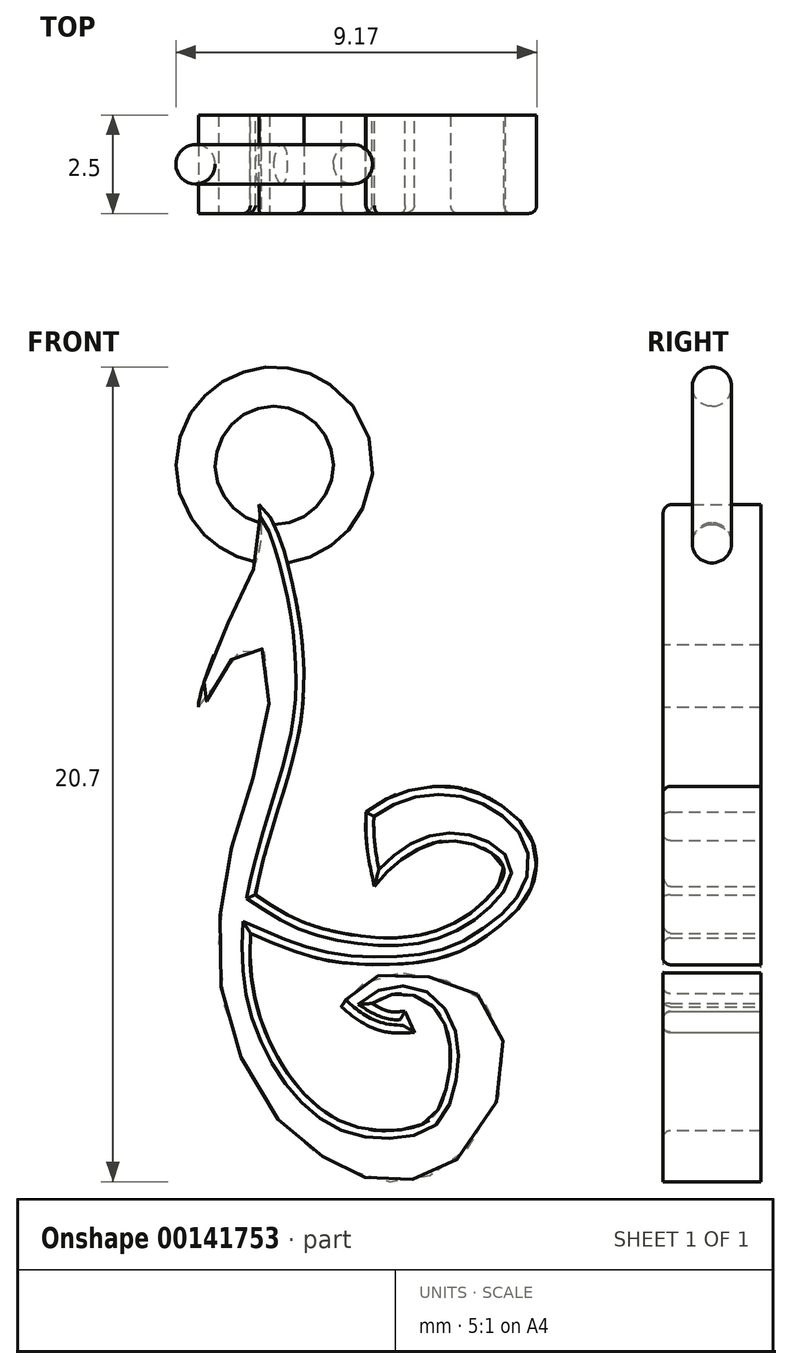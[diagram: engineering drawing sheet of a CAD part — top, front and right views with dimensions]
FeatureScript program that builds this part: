
annotation { "Feature Type Name" : "Feature", "Feature Type Description" : "" }
export const myFeature = defineFeature(function(context is Context, id is Id, definition is map)
    precondition{}
    {
        {
            var Q0;
            Q0=qCreatedBy(makeId("Front.planeOp"),FACE);
            var sketch = newSketch(context, id + "F0", { "sketchPlane" : qUnion([Q0])});
            skLineSegment(sketch, "E0.bottom", {"start": v(-7.5, 0) * mm, "end": v(9.5, 0) * mm, "construction": true});
            skLineSegment(sketch, "E0.top", {"start": v(-7.5, 17) * mm, "end": v(9.5, 17) * mm, "construction": true});
            skLineSegment(sketch, "E0.left", {"start": v(-7.5, 0) * mm, "end": v(-7.5, 17) * mm, "construction": true});
            skLineSegment(sketch, "E0.right", {"start": v(9.5, 0) * mm, "end": v(9.5, 17) * mm, "construction": true});
            skLineSegment(sketch, "E1", {"start": v(0, 0) * mm, "end": v(0, 23.23) * mm, "construction": true});
            skFitSpline(sketch, "E2", {"points": [v(-1.83, 17) * mm, v(-1.82, 15.9) * mm, v(-2.39, 14.45) * mm, v(-3.04, 13.02) * mm, v(-3.35, 11.84) * mm, v(-3.09, 12.13) * mm, v(-2.54, 13.05) * mm, v(-1.94, 13.43) * mm, v(-1.68, 13.22) * mm, v(-1.63, 11.44) * mm, v(-2.32, 9.03) * mm, v(-2.77, 6.94) * mm, v(-2.78, 4.69) * mm, v(-2.04, 2.45) * mm, v(-0.78, 0.82) * mm, v(0.2, 0.23) * mm, v(1.09, -0.16) * mm, v(2.12, -0.14) * mm, v(3.04, 0.23) * mm, v(4.24, 1.9) * mm, v(4.33, 3.53) * mm, v(3.7, 4.58) * mm, v(2.6, 4.98) * mm, v(1.43, 5.09) * mm, v(0.65, 4.7) * mm, v(0.26, 4.24) * mm], "startDerivative": vector(3.52, -28.57) * mm, "endDerivative": vector(-9.9, -17.08) * mm});
            skFitSpline(sketch, "E3", {"points": [v(0.26, 4.24) * mm, v(1.24, 3.64) * mm, v(2.12, 3.6) * mm], "startDerivative": vector(1.82, -1.62) * mm, "endDerivative": vector(1.77, 0.22) * mm});
            skLineSegment(sketch, "E4", {"start": v(2.12, 3.6) * mm, "end": v(1.89, 4.13) * mm});
            skFitSpline(sketch, "E5", {"points": [v(1.89, 4.13) * mm, v(1.46, 4.13) * mm, v(1.05, 4.33) * mm], "startDerivative": vector(-0.86, -0.08) * mm, "endDerivative": vector(-0.67, 0.39) * mm});
            skFitSpline(sketch, "E6", {"points": [v(1.05, 4.33) * mm, v(1.43, 4.53) * mm, v(2.2, 4.5) * mm, v(2.83, 3.93) * mm, v(3.04, 2.91) * mm, v(2.87, 1.98) * mm, v(2.5, 1.36) * mm, v(1.43, 1.1) * mm, v(0.23, 1.34) * mm, v(-0.95, 2.35) * mm, v(-1.8, 3.96) * mm, v(-2.06, 5.52) * mm, v(-1.92, 7.09) * mm, v(-1.38, 9.13) * mm, v(-0.75, 11.63) * mm, v(-0.8, 14.08) * mm, v(-1.14, 15.64) * mm, v(-1.44, 16.5) * mm, v(-1.83, 17) * mm], "startDerivative": vector(9.88, 7.94) * mm, "endDerivative": vector(-11.95, 7.75) * mm});
            skFitSpline(sketch, "E7", {"points": [v(-1.92, 7.09) * mm, v(-0.7, 6.4) * mm, v(1.22, 6) * mm, v(2.76, 6.2) * mm, v(3.76, 6.8) * mm, v(4.4, 7.67) * mm, v(4.1, 8.14) * mm, v(3.43, 8.42) * mm, v(2.66, 8.42) * mm, v(1.7, 7.91) * mm, v(1.1, 7.3) * mm], "startDerivative": vector(12.7, -8.61) * mm, "endDerivative": vector(-6.05, -7.17) * mm});
            skFitSpline(sketch, "E8", {"points": [v(1.1, 7.3) * mm, v(0.9, 8.5) * mm, v(0.9, 9.19) * mm], "startDerivative": vector(-0.46, 2.24) * mm, "endDerivative": vector(0.08, 1.5) * mm});
            skFitSpline(sketch, "E9", {"points": [v(-2.05, 6.11) * mm, v(-0.62, 5.55) * mm, v(0.65, 5.33) * mm, v(2.15, 5.37) * mm, v(3.39, 5.7) * mm, v(4.57, 6.55) * mm, v(5.04, 7.15) * mm, v(5.22, 7.9) * mm, v(4.96, 8.76) * mm, v(3.99, 9.56) * mm, v(2.88, 9.84) * mm, v(1.66, 9.64) * mm, v(0.9, 9.19) * mm], "startDerivative": vector(15.2, -6.57) * mm, "endDerivative": vector(-9.55, -6.77) * mm});
            skSolve(sketch);
        }
        {
            var Q0;
            Q0=qSketchRegion(id+"F0",true);
            extrude(context, id + "F1", {"entities" : qUnion([Q0]), "depth" : 2.5 * mm});
        }
        {
            var Q0;
            Q0=qCreatedBy(makeId("Right.planeOp"),FACE);
            cPlane(context, id + "F2", {"entities" : qUnion([Q0]), "cplaneType" : CPlaneType.OFFSET, "offset" : 1.44 * mm, "oppositeDirection" : true, "width" : 150 * mm, "height" : 150 * mm});
        }
        {
            var Q0;
            Q0=qCreatedBy(id+"F2.planeOp",FACE);
            var sketch = newSketch(context, id + "F3", { "sketchPlane" : qUnion([Q0])});
            skCircle(sketch, "E10", {"center": v(-1.25, 16) * mm, "radius": 0.5 * mm});
            skLineSegment(sketch, "E11", {"start": v(-3.17, 18) * mm, "end": v(2.9, 18) * mm, "construction": true});
            skSolve(sketch);
        }
        {
            var Q0;
            Q0=qSketchRegion(id+"F3",true);
            var Q1;
            Q1=sQuery(id+"F3.wireOp",EDGE,"E11");
            revolve(context, id + "F4", {"operationType" : NewBodyOperationType.ADD, "entities" : qUnion([Q0]), "axis" : qUnion([Q1]), "revolveType" : RevolveType.FULL});
        }
        {
            var Q0;
            {var subQ0=sQuery(id+"F0.wireOp",EDGE,"E6");Q0=makeQuery(id+"F1.opExtrude","CAP_EDGE",EDGE,{"disambiguationData":[OSD([subQ0]),TDD([makeQuery(id+"F0.imprint","IMPRINT",EDGE,{"disambiguationData":[TD([[makeQuery(id+"F0.imprint","INTERSECT",VERTEX,{"derivedFrom":[sQuery(id+"F0.wireOp",EDGE,"E5"),subQ0]}),-1.0]])],"derivedFrom":subQ0})])],"isStart":false});}
            var Q1;
            Q1=makeQuery(id+"F1.opExtrude","CAP_EDGE",EDGE,{"disambiguationData":[OSD([sQuery(id+"F0.wireOp",EDGE,"E5")])],"isStart":false});
            var Q2;
            Q2=makeQuery(id+"F1.opExtrude","CAP_EDGE",EDGE,{"disambiguationData":[OSD([sQuery(id+"F0.wireOp",EDGE,"E4")])],"isStart":false});
            var Q3;
            Q3=makeQuery(id+"F1.opExtrude","CAP_EDGE",EDGE,{"disambiguationData":[OSD([sQuery(id+"F0.wireOp",EDGE,"E3")])],"isStart":false});
            var Q4;
            Q4=makeQuery(id+"F1.opExtrude","CAP_EDGE",EDGE,{"disambiguationData":[OSD([sQuery(id+"F0.wireOp",EDGE,"E9")])],"isStart":false});
            var Q5;
            Q5=makeQuery(id+"F1.opExtrude","CAP_EDGE",EDGE,{"disambiguationData":[OSD([sQuery(id+"F0.wireOp",EDGE,"E8")])],"isStart":false});
            var Q6;
            Q6=makeQuery(id+"F1.opExtrude","CAP_EDGE",EDGE,{"disambiguationData":[OSD([sQuery(id+"F0.wireOp",EDGE,"E7")])],"isStart":false});
            var Q7;
            {var subQ0=sQuery(id+"F0.wireOp",EDGE,"E6");Q7=makeQuery(id+"F1.opExtrude","CAP_EDGE",EDGE,{"disambiguationData":[OSD([subQ0]),TDD([makeQuery(id+"F0.imprint","IMPRINT",EDGE,{"disambiguationData":[TD([[makeQuery(id+"F0.imprint","INTERSECT",VERTEX,{"derivedFrom":[sQuery(id+"F0.wireOp",EDGE,"E2"),subQ0]}),1.0]])],"derivedFrom":subQ0})])],"isStart":false});}
            fillet(context, id + "F5", {"entities" : qUnion([Q0, Q1, Q2, Q3, Q4, Q5, Q6, Q7]), "radius" : 0.2 * mm, "tangentPropagation" : true, "allowEdgeOverflow" : false});
        }
    });
